FCSTD DOCUMENT  (FreeCAD 0.20R29410 (Git))
Label: prancha-editavel-A2-modelo
License: All rights reserved
objects: Sketcher::SketchObject×1
note: 1 computed .brp shape members not serialized (recipe doc carries the construction recipe); baked Part::Feature solids carry a one-line shape summary decoded from their .brp

FEATURE [Sketcher::SketchObject] Sketch
  FullyConstrained = false
  sketch-geometry (12):
    g0: LineSegment StartX=-372.201 StartY=157.106 StartZ=0 EndX=221.799 EndY=157.106 EndZ=0
    g1: LineSegment StartX=221.799 StartY=157.106 StartZ=0 EndX=221.799 EndY=-262.894 EndZ=0
    g2: LineSegment StartX=221.799 StartY=-262.894 StartZ=0 EndX=-372.201 EndY=-262.894 EndZ=0
    g3: LineSegment StartX=-372.201 StartY=-262.894 StartZ=0 EndX=-372.201 EndY=157.106 EndZ=0
    g4: LineSegment StartX=211.799 StartY=-252.894 StartZ=0 EndX=31.7994 EndY=-252.894 EndZ=0
    g5: LineSegment StartX=31.7994 StartY=-252.894 StartZ=0 EndX=31.7994 EndY=-111.882 EndZ=0
    g6: LineSegment StartX=31.7994 StartY=-111.882 StartZ=0 EndX=211.799 EndY=-111.882 EndZ=0
    g7: LineSegment StartX=211.799 StartY=-111.882 StartZ=0 EndX=211.799 EndY=-252.894 EndZ=0
    g8: LineSegment StartX=-352.201 StartY=147.106 StartZ=0 EndX=211.799 EndY=147.106 EndZ=0
    g9: LineSegment StartX=211.799 StartY=147.106 StartZ=0 EndX=211.799 EndY=-252.894 EndZ=0
    g10: LineSegment StartX=211.799 StartY=-252.894 StartZ=0 EndX=-352.201 EndY=-252.894 EndZ=0
    g11: LineSegment StartX=-352.201 StartY=-252.894 StartZ=0 EndX=-352.201 EndY=147.106 EndZ=0
  constraints (33):
    c: Coincident(g0,g1)
    c: Coincident(g1,g2)
    c: Coincident(g2,g3)
    c: Coincident(g3,g0)
    c: Horizontal(g0)
    c: Horizontal(g2)
    c: Vertical(g1)
    c: Vertical(g3)
    c: DistanceX(g0,g0) = 594
    c: DistanceY(g2,g0) = 420
    c: Coincident(g4,g5)
    c: Coincident(g5,g6)
    c: Coincident(g6,g7)
    c: Coincident(g7,g4)
    c: Horizontal(g4)
    c: Horizontal(g6)
    c: Vertical(g5)
    c: Vertical(g7)
    c: DistanceX(g5,g6) = 180
    c: DistanceX(g4,g1) = 10
    c: DistanceY(g2,g4) = 10
    c: Coincident(g8,g9)
    c: Coincident(g9,g10)
    c: Coincident(g10,g11)
    c: Coincident(g11,g8)
    c: Horizontal(g8)
    c: Horizontal(g10)
    c: Vertical(g9)
    c: Vertical(g11)
    c: DistanceY(g8,g0) = 10
    c: DistanceY(g2,g10) = 10
    c: DistanceX(g8,g0) = 10
    c: DistanceX(g2,g10) = 20
